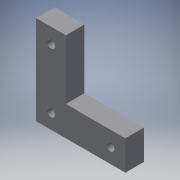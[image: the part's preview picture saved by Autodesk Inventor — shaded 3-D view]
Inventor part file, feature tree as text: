
AUTODESK INVENTOR PART (.ipt)
format: ipt  version: 2016 (Build 200138000, 138)  size: 106,496 bytes
history: native  units: in
note: dims shown in document units (in); Inventor stores cm internally (conversion verified against a paired STEP export)
features: extrude x1, sketch x1
ambient origin geometry x8: Origin, YZ Plane, XZ Plane, XY Plane, X Axis, Y Axis, Z Axis, Center Point
bodies: Solid1 (feature_tree)
feature tree (2):
  extrude  "Extrusion1"  Depth=3.0in
  sketch  "Sketch1"  dims[d0=3.0in d1=3.0in d2=2.0in d3=1.0in d4=0.2656in d5=0.2656in d6=0.2656in d7=0.5in d8=0.5in d9=0.5in d10=0.5in d11=0.5in d12=0.5in d13=0.625in d14=0.0in]
